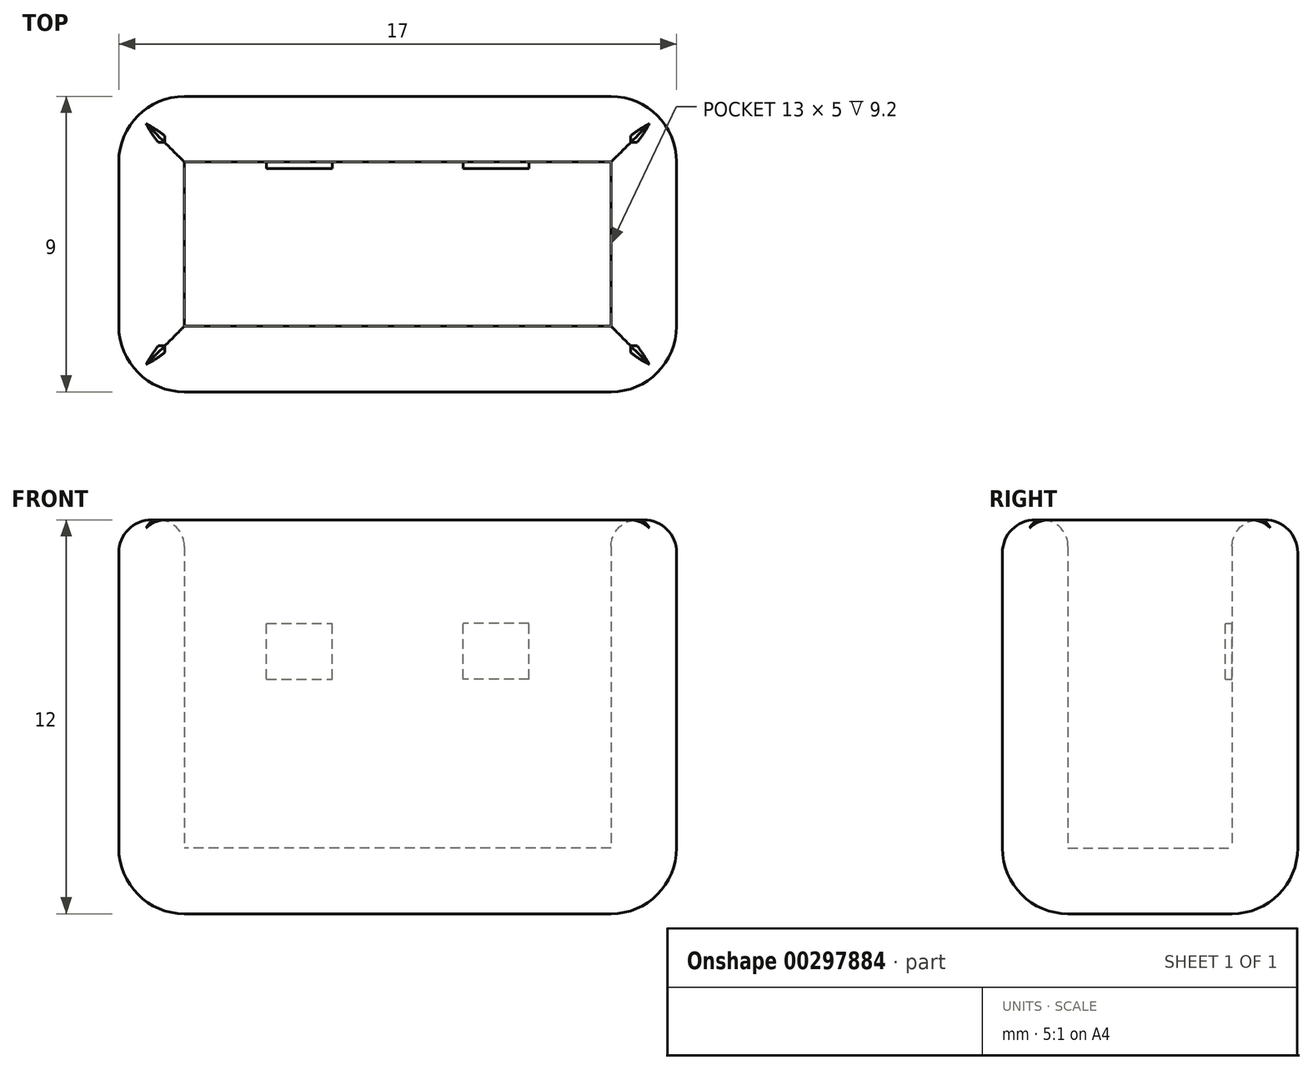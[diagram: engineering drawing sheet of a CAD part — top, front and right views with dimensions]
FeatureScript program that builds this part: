
annotation { "Feature Type Name" : "Feature", "Feature Type Description" : "" }
export const myFeature = defineFeature(function(context is Context, id is Id, definition is map)
    precondition{}
    {
        {
            var Q0;
            Q0=qCreatedBy(makeId("Top.planeOp"),FACE);
            var sketch = newSketch(context, id + "F0", { "sketchPlane" : qUnion([Q0])});
            skLineSegment(sketch, "E0.bottom", {"start": v(6.5, -2.5) * mm, "end": v(-6.5, -2.5) * mm});
            skLineSegment(sketch, "E0.top", {"start": v(6.5, 2.5) * mm, "end": v(-6.5, 2.5) * mm});
            skLineSegment(sketch, "E0.left", {"start": v(6.5, -2.5) * mm, "end": v(6.5, 2.5) * mm});
            skLineSegment(sketch, "E0.right", {"start": v(-6.5, -2.5) * mm, "end": v(-6.5, 2.5) * mm});
            skPoint(sketch, "E0.middle", {"position": v(0, 0) * mm});
            skLineSegment(sketch, "E1.0", {"start": v(8.5, -4.5) * mm, "end": v(-8.5, -4.5) * mm});
            skLineSegment(sketch, "E1.1", {"start": v(8.5, -4.5) * mm, "end": v(8.5, 4.5) * mm});
            skLineSegment(sketch, "E1.2", {"start": v(8.5, 4.5) * mm, "end": v(-8.5, 4.5) * mm});
            skLineSegment(sketch, "E1.3", {"start": v(-8.5, -4.5) * mm, "end": v(-8.5, 4.5) * mm});
            skSolve(sketch);
        }
        {
            var Q0;
            Q0=makeQuery(id+"F0.imprint","IMPRINT",FACE,{"disambiguationData":[TD([[makeQuery(id+"F0.imprint","IMPRINT",EDGE,{"derivedFrom":sQuery(id+"F0.wireOp",EDGE,"E0.bottom")}),1.0]])]});
            extrude(context, id + "F1", {"entities" : qUnion([Q0]), "depth" : 10 * mm});
        }
        {
            var Q0;
            Q0=makeQuery(id+"F1.opExtrude","SWEPT_EDGE",EDGE,{"disambiguationData":[OSD([sQuery(id+"F0.wireOp",EDGE,"E1.0"),sQuery(id+"F0.wireOp",EDGE,"E1.1")])]});
            var Q1;
            Q1=makeQuery(id+"F1.opExtrude","SWEPT_EDGE",EDGE,{"disambiguationData":[OSD([sQuery(id+"F0.wireOp",EDGE,"E1.1"),sQuery(id+"F0.wireOp",EDGE,"E1.2")])]});
            var Q2;
            Q2=makeQuery(id+"F1.opExtrude","SWEPT_EDGE",EDGE,{"disambiguationData":[OSD([sQuery(id+"F0.wireOp",EDGE,"E1.0"),sQuery(id+"F0.wireOp",EDGE,"E1.3")])]});
            var Q3;
            Q3=makeQuery(id+"F1.opExtrude","SWEPT_EDGE",EDGE,{"disambiguationData":[OSD([sQuery(id+"F0.wireOp",EDGE,"E1.2"),sQuery(id+"F0.wireOp",EDGE,"E1.3")])]});
            fillet(context, id + "F2", {"entities" : qUnion([Q0, Q1, Q2, Q3]), "radius" : 2 * mm, "tangentPropagation" : true, "allowEdgeOverflow" : false});
        }
        {
            var Q0;
            Q0=makeQuery(id+"F1.opExtrude","CAP_EDGE",EDGE,{"disambiguationData":[OSD([sQuery(id+"F0.wireOp",EDGE,"E1.0")])],"isStart":false});
            fillet(context, id + "F3", {"entities" : qUnion([Q0]), "radius" : 1 * mm, "tangentPropagation" : true, "allowEdgeOverflow" : false});
        }
        {
            var Q0;
            Q0=makeQuery(id+"F1.opExtrude","CAP_EDGE",EDGE,{"disambiguationData":[OSD([sQuery(id+"F0.wireOp",EDGE,"E0.bottom")])],"isStart":false});
            var Q1;
            Q1=makeQuery(id+"F1.opExtrude","CAP_EDGE",EDGE,{"disambiguationData":[OSD([sQuery(id+"F0.wireOp",EDGE,"E0.right")])],"isStart":false});
            var Q2;
            Q2=makeQuery(id+"F1.opExtrude","CAP_EDGE",EDGE,{"disambiguationData":[OSD([sQuery(id+"F0.wireOp",EDGE,"E0.top")])],"isStart":false});
            var Q3;
            Q3=makeQuery(id+"F1.opExtrude","CAP_EDGE",EDGE,{"disambiguationData":[OSD([sQuery(id+"F0.wireOp",EDGE,"E0.left")])],"isStart":false});
            fillet(context, id + "F4", {"entities" : qUnion([Q0, Q1, Q2, Q3]), "radius" : .8 * mm, "tangentPropagation" : true, "allowEdgeOverflow" : false});
        }
        {
            var Q0;
            Q0=makeQuery(id+"F1.opExtrude","CAP_FACE",FACE,{"disambiguationData":[OSD([sQuery(id+"F0.wireOp",EDGE,"E0.bottom"),sQuery(id+"F0.wireOp",EDGE,"E0.top"),sQuery(id+"F0.wireOp",EDGE,"E0.left"),sQuery(id+"F0.wireOp",EDGE,"E0.right"),sQuery(id+"F0.wireOp",EDGE,"E1.0"),sQuery(id+"F0.wireOp",EDGE,"E1.1"),sQuery(id+"F0.wireOp",EDGE,"E1.2"),sQuery(id+"F0.wireOp",EDGE,"E1.3")])],"isStart":true});
            var sketch = newSketch(context, id + "F5", { "sketchPlane" : qUnion([Q0])});
            skLineSegment(sketch, "E2.0", {"start": v(8.5, 2.5) * mm, "end": v(8.5, -2.5) * mm});
            skArc(sketch, "E3.0", {"start": v(6.5, -4.5) * mm, "mid": v(7.91, -3.91) * mm, "end": v(8.5, -2.5) * mm});
            skLineSegment(sketch, "E4.0", {"start": v(6.5, -4.5) * mm, "end": v(-6.5, -4.5) * mm});
            skArc(sketch, "E5.0", {"start": v(-8.5, -2.5) * mm, "mid": v(-7.91, -3.91) * mm, "end": v(-6.5, -4.5) * mm});
            skLineSegment(sketch, "E6.0", {"start": v(-8.5, 2.5) * mm, "end": v(-8.5, -2.5) * mm});
            skPoint(sketch, "E7.0", {"position": v(-7.91, 3.91) * mm});
            skArc(sketch, "E8.0", {"start": v(-6.5, 4.5) * mm, "mid": v(-7.91, 3.91) * mm, "end": v(-8.5, 2.5) * mm});
            skLineSegment(sketch, "E9.0", {"start": v(6.5, 4.5) * mm, "end": v(-6.5, 4.5) * mm});
            skArc(sketch, "E10.0", {"start": v(8.5, 2.5) * mm, "mid": v(7.91, 3.91) * mm, "end": v(6.5, 4.5) * mm});
            skSolve(sketch);
        }
        {
            var Q0;
            Q0 = qSketchRegion(id + "F5", true);
            extrude(context, id + "F6", {"entities" : qUnion([Q0]), "operationType" : NewBodyOperationType.ADD, "depth" : 2 * mm});
        }
        {
            var Q0;
            Q0=makeQuery(id+"F6.opExtrude","CAP_FACE",FACE,{"disambiguationData":[OSD([sQuery(id+"F5.wireOp",EDGE,"E2.0"),sQuery(id+"F5.wireOp",EDGE,"E3.0"),sQuery(id+"F5.wireOp",EDGE,"E4.0"),sQuery(id+"F5.wireOp",EDGE,"E5.0"),sQuery(id+"F5.wireOp",EDGE,"E6.0"),sQuery(id+"F5.wireOp",EDGE,"E8.0"),sQuery(id+"F5.wireOp",EDGE,"E9.0"),sQuery(id+"F5.wireOp",EDGE,"E10.0")])],"isStart":false});
            fillet(context, id + "F7", {"entities" : qUnion([Q0]), "radius" : 2 * mm, "tangentPropagation" : true, "allowEdgeOverflow" : false});
        }
        {
            var Q0;
            Q0=makeQuery(id+"F1.opExtrude","SWEPT_FACE",FACE,{"disambiguationData":[OSD([sQuery(id+"F0.wireOp",EDGE,"E0.top")])]});
            var sketch = newSketch(context, id + "F8", { "sketchPlane" : qUnion([Q0])});
            skLineSegment(sketch, "E11.bottom", {"start": v(-4, 5.15) * mm, "end": v(-2, 5.15) * mm});
            skLineSegment(sketch, "E11.top", {"start": v(-4, 6.85) * mm, "end": v(-2, 6.85) * mm});
            skLineSegment(sketch, "E11.left", {"start": v(-4, 5.15) * mm, "end": v(-4, 6.85) * mm});
            skLineSegment(sketch, "E11.right", {"start": v(-2, 5.15) * mm, "end": v(-2, 6.85) * mm});
            skLineSegment(sketch, "E12.MirrorCS", {"start": v(2, 5.15) * mm, "end": v(2, 6.85) * mm});
            skLineSegment(sketch, "E13.MirrorCS", {"start": v(4, 6.85) * mm, "end": v(2, 6.85) * mm});
            skLineSegment(sketch, "E14.MirrorCS", {"start": v(4, 5.15) * mm, "end": v(2, 5.15) * mm});
            skLineSegment(sketch, "E15.MirrorCS", {"start": v(4, 5.15) * mm, "end": v(4, 6.85) * mm});
            skSolve(sketch);
        }
        {
            var Q0;
            Q0 = qSketchRegion(id + "F8", true);
            extrude(context, id + "F9", {"entities" : qUnion([Q0]), "operationType" : NewBodyOperationType.ADD, "depth" : .2 * mm});
        }
    });
